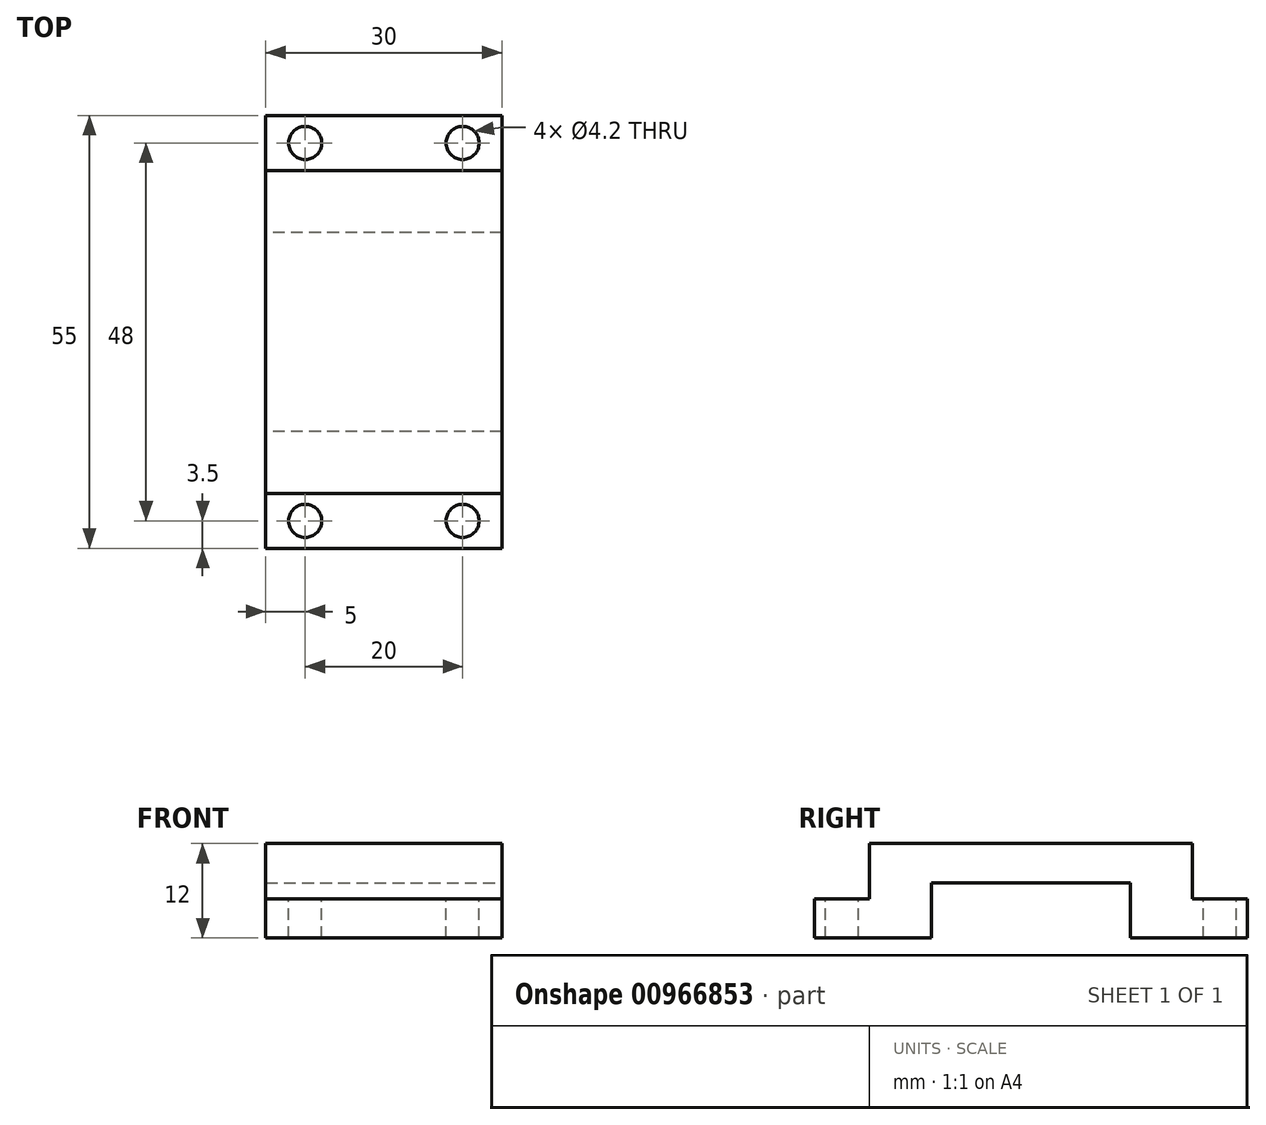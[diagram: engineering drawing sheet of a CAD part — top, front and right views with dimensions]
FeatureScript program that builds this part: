
annotation { "Feature Type Name" : "Feature", "Feature Type Description" : "" }
export const myFeature = defineFeature(function(context is Context, id is Id, definition is map)
    precondition{}
    {
        {
            var Q0;
            Q0=qCreatedBy(makeId("Top.planeOp"),FACE);
            var sketch = newSketch(context, id + "F0", { "sketchPlane" : qUnion([Q0])});
            skLineSegment(sketch, "E0.bottom", {"start": v(15, -27.5) * mm, "end": v(-15, -27.5) * mm});
            skLineSegment(sketch, "E0.top", {"start": v(15, 27.5) * mm, "end": v(-15, 27.5) * mm});
            skLineSegment(sketch, "E0.left", {"start": v(15, -27.5) * mm, "end": v(15, 27.5) * mm});
            skLineSegment(sketch, "E0.right", {"start": v(-15, -27.5) * mm, "end": v(-15, 27.5) * mm});
            skPoint(sketch, "E0.middle", {"position": v(0, 0) * mm});
            skSolve(sketch);
        }
        {
            var Q0;
            Q0 = qSketchRegion(id + "F0", true);
            extrude(context, id + "F1", {"entities" : qUnion([Q0]), "depth" : 12 * mm, "offsetDistance" : 25 * mm});
        }
        {
            var Q0;
            Q0=qCreatedBy(makeId("Right.planeOp"),FACE);
            cPlane(context, id + "F2", {"entities" : qUnion([Q0]), "cplaneType" : CPlaneType.OFFSET, "offset" : 15 * mm, "width" : 150 * mm, "height" : 150 * mm});
        }
        {
            var Q0;
            Q0=qCreatedBy(id+"F2.planeOp",FACE);
            var sketch = newSketch(context, id + "F3", { "sketchPlane" : qUnion([Q0])});
            skLineSegment(sketch, "E1.bottom", {"start": v(12.65, -7) * mm, "end": v(-12.65, -7) * mm});
            skLineSegment(sketch, "E1.top", {"start": v(12.65, 7) * mm, "end": v(-12.65, 7) * mm});
            skLineSegment(sketch, "E1.left", {"start": v(12.65, -7) * mm, "end": v(12.65, 7) * mm});
            skLineSegment(sketch, "E1.right", {"start": v(-12.65, -7) * mm, "end": v(-12.65, 7) * mm});
            skPoint(sketch, "E1.middle", {"position": v(0, 0) * mm});
            skSolve(sketch);
        }
        {
            var Q0;
            Q0 = qSketchRegion(id + "F3", true);
            extrude(context, id + "F4", {"entities" : qUnion([Q0]), "operationType" : NewBodyOperationType.REMOVE, "endBound" : BoundingType.THROUGH_ALL, "oppositeDirection" : true, "depth" : 25 * mm, "offsetDistance" : 25 * mm});
        }
        {
            var Q0;
            Q0=makeQuery(id+"F1.opExtrude","SWEPT_FACE",FACE,{"disambiguationData":[OSD([sQuery(id+"F0.wireOp",EDGE,"E0.left")])]});
            var sketch = newSketch(context, id + "F5", { "sketchPlane" : qUnion([Q0])});
            skLineSegment(sketch, "E2.bottom", {"start": v(-27.5, 12) * mm, "end": v(-20.5, 12) * mm});
            skLineSegment(sketch, "E2.top", {"start": v(-27.5, 5) * mm, "end": v(-20.5, 5) * mm});
            skLineSegment(sketch, "E2.left", {"start": v(-27.5, 12) * mm, "end": v(-27.5, 5) * mm});
            skLineSegment(sketch, "E2.right", {"start": v(-20.5, 12) * mm, "end": v(-20.5, 5) * mm});
            skSolve(sketch);
        }
        {
            var Q0;
            Q0 = qSketchRegion(id + "F5", true);
            extrude(context, id + "F6", {"entities" : qUnion([Q0]), "operationType" : NewBodyOperationType.REMOVE, "endBound" : BoundingType.THROUGH_ALL, "oppositeDirection" : true, "depth" : 25 * mm, "offsetDistance" : 25 * mm});
        }
        {
            var Q0;
            Q0=makeQuery(id+"F1.opExtrude","SWEPT_FACE",FACE,{"disambiguationData":[OSD([sQuery(id+"F0.wireOp",EDGE,"E0.left")])]});
            var sketch = newSketch(context, id + "F7", { "sketchPlane" : qUnion([Q0])});
            skLineSegment(sketch, "E3.bottom", {"start": v(27.5, 12) * mm, "end": v(20.5, 12) * mm});
            skLineSegment(sketch, "E3.top", {"start": v(27.5, 5) * mm, "end": v(20.5, 5) * mm});
            skLineSegment(sketch, "E3.left", {"start": v(27.5, 12) * mm, "end": v(27.5, 5) * mm});
            skLineSegment(sketch, "E3.right", {"start": v(20.5, 12) * mm, "end": v(20.5, 5) * mm});
            skSolve(sketch);
        }
        {
            var Q0;
            Q0 = qSketchRegion(id + "F7", true);
            extrude(context, id + "F8", {"entities" : qUnion([Q0]), "operationType" : NewBodyOperationType.REMOVE, "endBound" : BoundingType.THROUGH_ALL, "oppositeDirection" : true, "depth" : 25 * mm, "offsetDistance" : 25 * mm});
        }
        {
            var Q0;
            Q0=qCreatedBy(makeId("Top.planeOp"),FACE);
            cPlane(context, id + "F9", {"entities" : qUnion([Q0]), "cplaneType" : CPlaneType.OFFSET, "offset" : 5 * mm, "width" : 150 * mm, "height" : 150 * mm});
        }
        {
            var Q0;
            Q0=qCreatedBy(id+"F9.planeOp",FACE);
            var sketch = newSketch(context, id + "F10", { "sketchPlane" : qUnion([Q0])});
            skPoint(sketch, "E4", {"position": v(-15, 24) * mm});
            skLineSegment(sketch, "E5", {"start": v(-15, 24) * mm, "end": v(15, 24) * mm, "construction": true});
            skPoint(sketch, "E6", {"position": v(-10, 24) * mm});
            skPoint(sketch, "E7", {"position": v(10, 24) * mm});
            skCircle(sketch, "E8", {"center": v(-10, 24) * mm, "radius": 2.1 * mm});
            skCircle(sketch, "E9", {"center": v(10, 24) * mm, "radius": 2.1 * mm});
            skSolve(sketch);
        }
        {
            var Q0;
            Q0 = qSketchRegion(id + "F10", true);
            extrude(context, id + "F11", {"entities" : qUnion([Q0]), "operationType" : NewBodyOperationType.REMOVE, "endBound" : BoundingType.THROUGH_ALL, "oppositeDirection" : true, "depth" : 25 * mm, "offsetDistance" : 25 * mm});
        }
        {
            var Q0;
            Q0=makeQuery(id+"F6.boolean.opBoolean","COPY",FACE,{"derivedFrom":makeQuery(id+"F6.opExtrude","SWEPT_FACE",FACE,{"disambiguationData":[OSD([sQuery(id+"F5.wireOp",EDGE,"E2.top")])]})});
            var sketch = newSketch(context, id + "F12", { "sketchPlane" : qUnion([Q0])});
            skLineSegment(sketch, "E10", {"start": v(-15, -24) * mm, "end": v(15, -24) * mm, "construction": true});
            skPoint(sketch, "E11", {"position": v(-10, -24) * mm});
            skPoint(sketch, "E12", {"position": v(10, -24) * mm});
            skCircle(sketch, "E13", {"center": v(-10, -24) * mm, "radius": 2.1 * mm});
            skCircle(sketch, "E14", {"center": v(10, -24) * mm, "radius": 2.1 * mm});
            skSolve(sketch);
        }
        {
            var Q0;
            Q0 = qSketchRegion(id + "F12", true);
            extrude(context, id + "F13", {"entities" : qUnion([Q0]), "operationType" : NewBodyOperationType.REMOVE, "endBound" : BoundingType.THROUGH_ALL, "oppositeDirection" : true, "depth" : 25 * mm, "offsetDistance" : 25 * mm});
        }
    });
